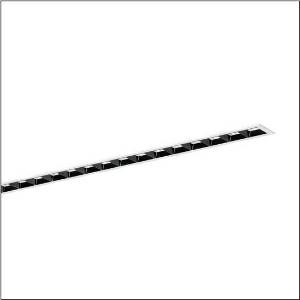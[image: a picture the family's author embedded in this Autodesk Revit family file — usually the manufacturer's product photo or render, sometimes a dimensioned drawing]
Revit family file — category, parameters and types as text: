
# Revit family: silica_r__21_51mx14da34wb_b271
name_source: partatom
category: Lighting Fixtures
units: mm (PartAtom-declared; Revit-internal decimal feet)

## family parameters
Cut with Voids When Loaded = No
Host = Face
Light Source = No
Part Type = Normal
Room Calculation Point = No
Round Connector Dimension = Use Diameter
Shared = No

## types (1)
- --- (1 x LED, 4320 lm, 32.1 W, 3000K)
    Apparent Load = 32 VA
    CIE Flux Codes = 74 94 99 100 100
    Color Rendering = 80
    Color Temperature = 3000K
    Default Elevation = 1800 mm
    Description = Silica® 21, office luminaire, primary light control with darklight reflector, of PMMA, black, light emission: direct distribution, primary light characteristic: asymmetric, installation type: recessed, LED, rated luminous flux: 4.320lm, luminous efficacy: 135lm/W, light colour: 830, colour temperature: 3000K, with terminal, 3+2-pole, max. 2.5mm², mains connection: 220..240V, AC, 50/60Hz, rated input power: 32.1W, luminaire housing, of aluminium, traffic white (RAL 9016), length: 1.228mm, width: 79mm, height: 53mm, protection rating (complete): IP20, insulation class (complete): insulation class I (protective earthing), certification: CE, permissible operating ambient temperature: 0..+35°C, standard: EN 50419, packaging unit: 1 piece
    Height = 0 mm  [stored 0 ft]
    Lamp = 1 x LED
    Lamp Light Flux = 4320 lm
    Lamp Power = 32.1 W
    Lamp count = 1
    Length = 1227 mm
    Luminous efficacy = 135 lm/W
    Manufacturer = Siteco
    ModVariant = No
    Model = 51MX14DA34WB
    Mounting Place = Ceiling
    Mounting Type = Recessed
    Number of Poles = 1
    OnlyDefault = Yes
    Power Factor = 1
    Product Name = Silica® 21
    Product group = office luminaire | ceiling recessed
    ProductGroupID = 400
    Protection Class = Protection class I
    Protection Degree = IP 20
    RLX_Detail_Level = 1
    RlxData = <blob elided: 39277 chars, md5=db20dd97>
    Socket = socket
    Standby Power = 0 W
    System Light Flux = 4320 lm
    System Power = 32 W
    Type Comments = factory setting: luminous flux: 100 % | dim-lin: 254 | 448 mA
    Type Image = l_1251632.jpg
    URL = http://relux.com
    VarID = @adj_031673
    Voltage = 0 V
    Weight = 0.00 kg
    Width = 79 mm

note: [stored X ft] marks values corroborated as IEEE doubles in the binary element streams (Revit-internal decimal feet)

## geometry (parser evidence)
native form markers: Blend x4, Sweep x10
no freeform markers — native parametric forms only
